FCSTD DOCUMENT  (FreeCAD 0.16R6706 (Git))
Label: press_01
License: All rights reserved
LicenseURL: http://en.wikipedia.org/wiki/All_rights_reserved
objects: Sketcher::SketchObject×1
note: 1 computed .brp shape members not serialized (recipe doc carries the construction recipe); baked Part::Feature solids carry a one-line shape summary decoded from their .brp

FEATURE [Sketcher::SketchObject] Sketch
  sketch-geometry (29):
    g0: Circle CenterX=3274.57 CenterY=-325.477 CenterZ=0 NormalX=0 NormalY=0 NormalZ=1 Radius=683.638
    g1: LineSegment StartX=3274.57 StartY=-325.477 StartZ=0 EndX=2591.59 EndY=-355.478 EndZ=0
    g2: LineSegment StartX=222.815 StartY=383.28 StartZ=0 EndX=222.815 EndY=-1.91553 EndZ=0
    g3: LineSegment StartX=222.815 StartY=-1.91553 StartZ=0 EndX=225.997 EndY=-5.09751 EndZ=0
    g4: LineSegment StartX=225.997 StartY=-5.09751 StartZ=0 EndX=564.634 EndY=-5.09751 EndZ=0
    g5: LineSegment StartX=564.634 StartY=-5.09751 StartZ=0 EndX=564.634 EndY=-108.166 EndZ=0
    g6: LineSegment StartX=564.634 StartY=-108.166 StartZ=0 EndX=225.997 EndY=-108.166 EndZ=0
    g7: LineSegment StartX=225.997 StartY=-108.166 StartZ=0 EndX=222.815 EndY=-111.348 EndZ=0
    g8: LineSegment StartX=222.815 StartY=-111.348 StartZ=0 EndX=222.815 EndY=-496.544 EndZ=0
    g9: LineSegment StartX=222.815 StartY=-496.544 StartZ=0 EndX=1590.09 EndY=-496.544 EndZ=0
    g10: LineSegment StartX=1590.09 StartY=-496.544 StartZ=0 EndX=1590.09 EndY=-111.348 EndZ=0
    g11: LineSegment StartX=1590.09 StartY=-111.348 StartZ=0 EndX=1586.91 EndY=-108.166 EndZ=0
    g12: LineSegment StartX=1586.91 StartY=-108.166 StartZ=0 EndX=1248.27 EndY=-108.166 EndZ=0
    g13: LineSegment StartX=1248.27 StartY=-108.166 StartZ=0 EndX=1248.27 EndY=-5.09751 EndZ=0
    g14: LineSegment StartX=1248.27 StartY=-5.09751 StartZ=0 EndX=1586.91 EndY=-5.09751 EndZ=0
    g15: LineSegment StartX=1586.91 StartY=-5.09751 StartZ=0 EndX=1590.09 EndY=-1.91553 EndZ=0
    g16: LineSegment StartX=1590.09 StartY=-1.91553 StartZ=0 EndX=1590.09 EndY=383.28 EndZ=0
    g17: LineSegment StartX=1590.09 StartY=383.28 StartZ=0 EndX=222.815 EndY=383.28 EndZ=0
    g18: GeomPoint [constr] X=906.453 Y=383.28 Z=0
    g19: LineSegment StartX=906.453 StartY=383.28 StartZ=0 EndX=906.453 EndY=-496.544 EndZ=0
    g20: GeomPoint [constr] X=906.453 Y=-56.6317 Z=0
    g21: LineSegment StartX=906.453 StartY=-56.6317 StartZ=0 EndX=222.815 EndY=-56.6317 EndZ=0
    g22: LineSegment StartX=2937.53 StartY=-391.866 StartZ=0 EndX=2933.01 EndY=-288.897 EndZ=0
    g23: LineSegment StartX=2937.53 StartY=-391.866 StartZ=0 EndX=2599.22 EndY=-406.727 EndZ=0
    g24: LineSegment StartX=2933.01 StartY=-288.897 StartZ=0 EndX=2594.7 EndY=-303.758 EndZ=0
    g25: GeomPoint [constr] X=2935.27 Y=-340.381 Z=0
    g26: LineSegment StartX=2599.22 StartY=-406.727 StartZ=0 EndX=2596.18 EndY=-410.045 EndZ=0
    g27: LineSegment StartX=2594.7 StartY=-303.758 StartZ=0 EndX=2591.38 EndY=-300.718 EndZ=0
    g28: GeomPoint [constr] X=564.634 Y=-56.6317 Z=0
  constraints (77):
    c: Coincident(g1,g0)
    c: PointOnObject(g1,g0)
    c: Coincident(g2,g3)
    c: Coincident(g3,g4)
    c: Coincident(g4,g5)
    c: Coincident(g5,g6)
    c: Horizontal(g6)
    c: Coincident(g6,g7)
    c: Coincident(g7,g8)
    c: Coincident(g8,g9)
    c: Horizontal(g9)
    c: Coincident(g9,g10)
    c: Coincident(g10,g11)
    c: Coincident(g11,g12)
    c: Coincident(g12,g13)
    c: Vertical(g13)
    c: Coincident(g13,g14)
    c: Horizontal(g14)
    c: Coincident(g14,g15)
    c: Coincident(g15,g16)
    c: Coincident(g16,g17)
    c: Coincident(g17,g2)
    c: Parallel(g17,g9)
    c: Parallel(g8,g2)
    c: Parallel(g2,g10)
    c: Parallel(g10,g16)
    c: Perpendicular(g16,g17)
    c: Equal(g16,g10)
    c: Equal(g10,g2)
    c: Equal(g4,g6)
    c: Equal(g6,g14)
    c: Perpendicular(g2,g4)
    c: Perpendicular(g4,g5)
    c: Equal(g14,g12)
    c: Equal(g13,g5)
    c: Equal(g12,g14)
    c: Perpendicular(g12,g13)
    c: Angle(g8,g7) = 2.35619
    c: Equal(g7,g11)
    c: Equal(g11,g3)
    c: Equal(g3,g15)
    c: Angle(g4,g3) = 2.35619
    c: Angle(g12,g11) = 2.35619
    c: Angle(g15,g14) = 2.35619
    c: Distance(g3) = 4.5
    c: PointOnObject(g18,g17)
    c: Symmetric(g17,g17,g18)
    c: Coincident(g19,g18)
    c: PointOnObject(g19,g9)
    c: Perpendicular(g17,g19)
    c: PointOnObject(g20,g19)
    c: Symmetric(g19,g19,g20)
    c: Coincident(g21,g20)
    c: Horizontal(g21)
    c: PointOnObject(g21,g8)
    c: Equal(g21,g1)
    c: Perpendicular(g1,g22)
    c: Equal(g22,g13)
    c: Symmetric(g22,g22,g1)
    c: Coincident(g23,g22)
    c: Perpendicular(g23,g22)
    c: Coincident(g24,g22)
    c: Perpendicular(g22,g24)
    c: PointOnObject(g25,g1)
    c: PointOnObject(g25,g22)
    c: Coincident(g26,g23)
    c: PointOnObject(g26,g0)
    c: Coincident(g27,g24)
    c: PointOnObject(g27,g0)
    c: Angle(g26,g23) = 2.35619
    c: Angle(g24,g27) = 2.35619
    c: Distance(g27) = 4.5
    c: Equal(g26,g27)
    c: Equal(g14,g23)
    c: PointOnObject(g28,g5)
    c: PointOnObject(g28,g21)
    c: Symmetric(g21,g21,g28)
